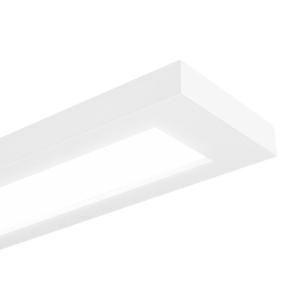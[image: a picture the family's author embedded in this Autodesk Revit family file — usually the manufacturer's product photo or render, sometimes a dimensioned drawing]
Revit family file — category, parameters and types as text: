
# Revit family: 3f_filippi_-_3f_travetta_op_3f_filippi_-_10777_-_3f_travetta_led_2x40w_op_l2200
name_source: partatom
category: Lighting Fixtures
units: mm (PartAtom-declared; Revit-internal decimal feet)

## family parameters
Cut with Voids When Loaded = No
Host = Face
Light Source = No
Part Type = Normal
Room Calculation Point = No
Round Connector Dimension = Use Diameter
Shared = No

## types (1)
- 3F Filippi - 3F Travetta OP (1 x LED, 9511 lm, 90 W, 4000 K)
    Apparent Load = 90 VA
    Approval mark = ENEC
    CIE Flux Codes = 49 81 97 100 100
    Color Rendering = 80
    Color Temperature = 4000 K
    Control Gear = Electronic ballast
    Default Elevation = 1800 mm
    Description = ILLUMINOTECHNICAL
Luminous efficiency 100% (DLOR 100%, ULOR 0%).
Initial luminous flux of the luminaire 9511 lm.
Direct symmetric distribution.
Installation Interdistance Transv.D = 1.19 x hu - Long.D = 1.20 x hu.
Tabular UGR (CIE 117 - 4H-8H; S=0.25H; 70/50/20): RUG 23.9 - 24.7.
Beam angle: 104° - 107°.
Luminous efficacy 106 lm/W.
Lifetime (L93/B10): 30000 h. (tq+25°C)
Lifetime (L90/B10): 50000 h. (tq+25°C)
Lifetime (L85/B10): 80000 h. (tq+25°C)
Lifetime (L80/B10): 100000 h. (tq+25°C)
Sudden decreased luminous flux after 50000 hours: 0% (C0).
Photobiological safety in compliance with IEC/TR 62778: RG0 risk exempt, (IEC 62471).
In compliance with IEC/EN 62722-2-1 - IEC/EN 62717 standards.

SOURCE
2 linear LED modules 40W/840.
Energy efficiency class (UE 2019/2020 - UE 2019/2015): D.
CIE 13.3 Colour rendering index: CRI >80 (R9 <50%).
IES TM-30 Fidelity Index: Rf = 84 Rg = 95.
CCT nominal colour temperature 4000 K.
Colour initial tolerance (MacAdam): SDCM 2.

MECHANICAL
Housing with squared shape in white painted galvannealed steel, with nonreflecting surface.
Flow recuperator in semi-glossy aluminium.
Opal methacrylate (PMMA) flat diffuser, anti-glare.
Luminaire with limited surface temperature. - D - (EN 60598-2-24)
Dimensions: 2200x190 mm, height 60 mm (edge 40 mm). Weight 7.845 kg.
IP20 protection degree.
Glow-wire test resistance 650°C.

ELECTRICAL
Halogen Free electronic wiring 230V-50/60Hz, power factor 0.95, THD <25%, constant output current, SELV, class I, 2 driver.
Power of the luminaire 90 W.
CE - IEC 60598-1 - EN 60598-1.
SAFE FLICKER: PstLM=<1 and SVM=<0.4 (IEC TR 61547-1 and IEC TR 63158), to ensure a more comfortable and safe light.
Luminaire compliant with EN 60598-2-22 for power supply from a centralised emergency system CPSS (Central Power Supply System), not incorporated in the luminaire - high risk areas excluded. The default power and flux are 100% in AC and 100% in DC.
Ambient temperature from 0°C to +25°C.
Temperature class T6 max 85°C.
Relative humidity UR: <85%.

INSTALLATION
Ceiling / Suspended.
All accessories dedicated to this product are available on the Catalog and on our website www.3F-Filippi.com.

APPLICATIONS
In environments, even with reduced height, requiring a comfortable light.
Exhibitions area, halls, great halls and shops.

WARNING
Luminaire designed for disposal/recycling at end-of-life.
Replaceable (LED only) light source by a professional. Replaceable control gear by a professional.
    Height = 60 mm  [stored 0.19685 ft]
    Lamp = 1 x LED
    Lamp Light Flux = 9511 lm
    Lamp Power = 90 W
    Lamp count = 1
    Length = 2200 mm
    Lifetime = 50000 h
    Luminous efficacy = 106 lm/W
    Manufacturer = 3F Filippi
    ModVariant = No
    Model = 3F Filippi - 10777 - 3F Travetta LED 2x40W OP L2200
    Mounting Place = Ceiling
    Mounting Type = Pendant
    Number of Poles = 1
    OnlyDefault = Yes
    Power Factor = 1
    Product Name = 3F Filippi - 3F Travetta OP
    Product group = pendant luminaire
    ProductGroupID = 9
    Protection Class = Protection class I
    Protection Degree = IP 20
    RLX_Detail_Level = 1
    RLX_Emergency_Light_Flux = 0 lm
    RLX_Emergency_Type = 0
    RLX_Emergency_Type_DB = No
    RlxData = <blob elided: 35861 chars, md5=ca4f1f67>
    Socket = socket
    Standby Power = 0 W
    System Light Flux = 9511 lm
    System Power = 90 W
    Type Comments = Product without accessories
    Type Image = 3ffilippi_3f_travetta_led_op.jpg
    URL = http://relux.com
    VarID = ---
    Voltage = 0 V
    Weight = 0.00 kg
    Width = 190 mm  [stored 0.62336 ft]

note: [stored X ft] marks values corroborated as IEEE doubles in the binary element streams (Revit-internal decimal feet)

## geometry (parser evidence)
native form markers: Blend x4, Sweep x10
no freeform markers — native parametric forms only
